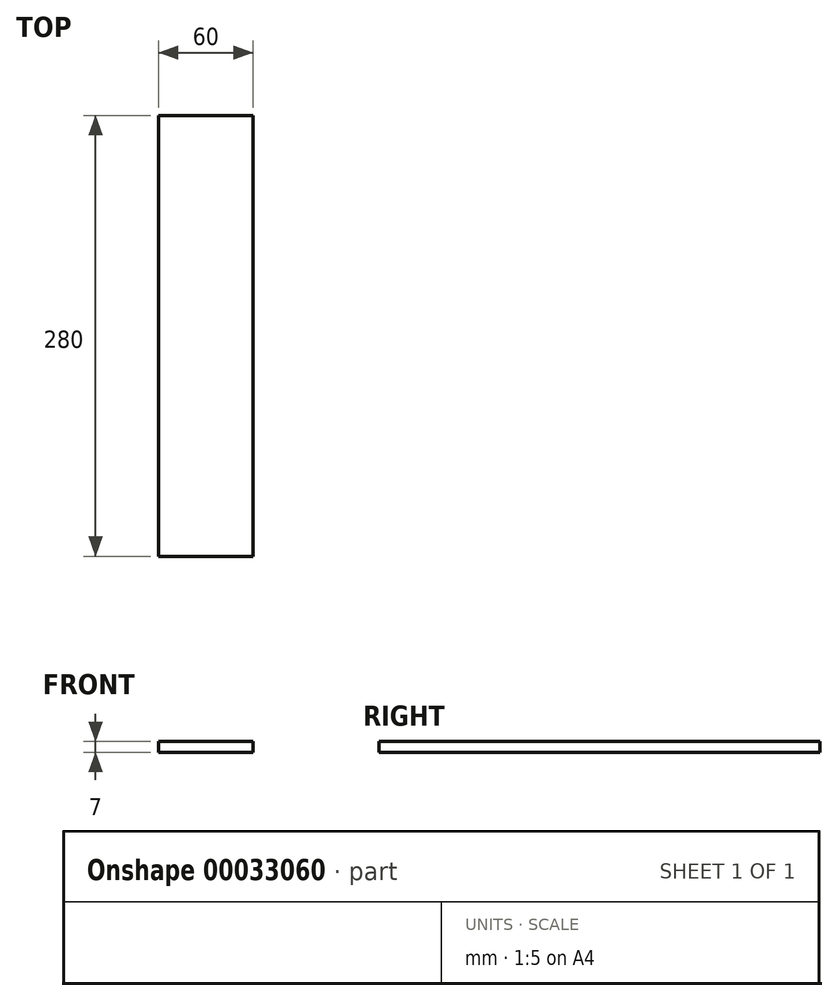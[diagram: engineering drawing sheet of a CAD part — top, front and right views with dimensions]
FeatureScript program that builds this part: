
annotation { "Feature Type Name" : "Feature", "Feature Type Description" : "" }
export const myFeature = defineFeature(function(context is Context, id is Id, definition is map)
    precondition{}
    {
        {
            var Q0;
            Q0=qCreatedBy(makeId("Top.planeOp"),FACE);
            var sketch = newSketch(context, id + "F0", { "sketchPlane" : qUnion([Q0])});
            skLineSegment(sketch, "E0.bottom", {"start": v(0, 0) * mm, "end": v(60, 0) * mm});
            skLineSegment(sketch, "E0.top", {"start": v(0, 280) * mm, "end": v(60, 280) * mm});
            skLineSegment(sketch, "E0.left", {"start": v(0, 0) * mm, "end": v(0, 280) * mm});
            skLineSegment(sketch, "E0.right", {"start": v(60, 0) * mm, "end": v(60, 280) * mm});
            skSolve(sketch);
        }
        {
            var Q0;
            Q0=makeQuery(id+"F0.imprint","IMPRINT",FACE,{"disambiguationData":[TD([[makeQuery(id+"F0.imprint","IMPRINT",EDGE,{"derivedFrom":sQuery(id+"F0.wireOp",EDGE,"E0.bottom")}),1.0]])]});
            extrude(context, id + "F1", {"entities" : qUnion([Q0]), "depth" : 7 * mm});
        }
    });
